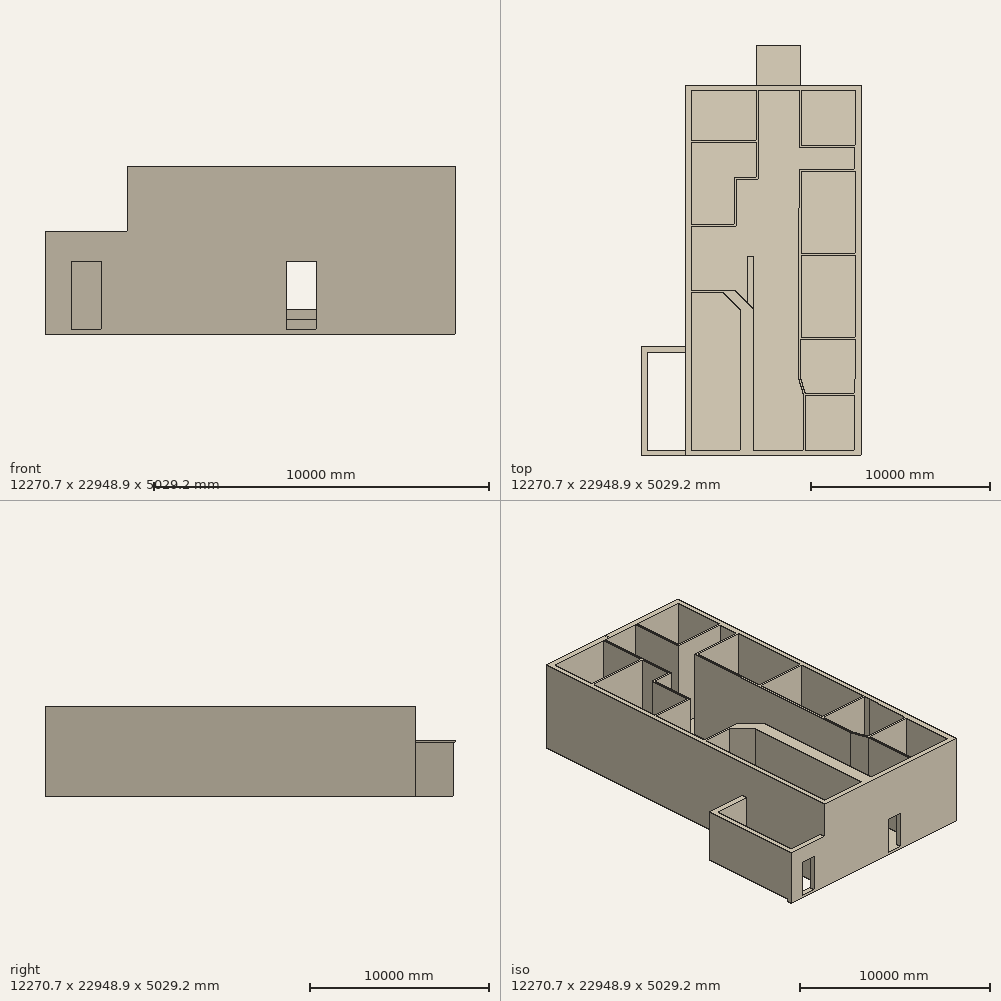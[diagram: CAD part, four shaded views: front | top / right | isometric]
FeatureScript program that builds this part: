
annotation { "Feature Type Name" : "Feature", "Feature Type Description" : "" }
export const myFeature = defineFeature(function(context is Context, id is Id, definition is map)
    precondition{}
    {
        {
            var Q0;
            Q0=qCreatedBy(makeId("Top.planeOp"),FACE);
            var sketch = newSketch(context, id + "F0", { "sketchPlane" : qUnion([Q0])});
            skLineSegment(sketch, "E0.left", {"start": v(4876.8, -10061.6) * mm, "end": v(4876.8, -6899.3) * mm});
            skLineSegment(sketch, "E0.right", {"start": v(2019.3, -10073.92) * mm, "end": v(2019.3, -7013.6) * mm});
            skLineSegment(sketch, "E1.left", {"start": v(4876.8, -6899.3) * mm, "end": v(4930.14, -4203.7) * mm});
            skLineSegment(sketch, "E2.top", {"start": v(4930.14, 835) * mm, "end": v(1882.14, 835) * mm});
            skLineSegment(sketch, "E2.left", {"start": v(4930.14, -4203.7) * mm, "end": v(4930.14, -3851.3) * mm});
            skLineSegment(sketch, "E3.bottom", {"start": v(1882.14, 835) * mm, "end": v(4930.14, 835) * mm});
            skLineSegment(sketch, "E4.bottom", {"start": v(-4267.2, -10061.6) * mm, "end": v(-1524, -10061.6) * mm});
            skLineSegment(sketch, "E4.left", {"start": v(-4267.2, -10061.6) * mm, "end": v(-4267.2, -1222.4) * mm});
            skLineSegment(sketch, "E5", {"start": v(-4267.2, -1222.4) * mm, "end": v(-2489.53, -1222.4) * mm});
            skLineSegment(sketch, "E6.top", {"start": v(-609.6, 5216.5) * mm, "end": v(-1828.8, 5216.5) * mm});
            skLineSegment(sketch, "E6.right", {"start": v(-1828.8, 2574.9) * mm, "end": v(-1828.8, 5216.5) * mm});
            skLineSegment(sketch, "E7", {"start": v(-4267.2, 2574.9) * mm, "end": v(-1828.8, 2574.9) * mm});
            skLineSegment(sketch, "E8", {"start": v(2133.6, -10061.6) * mm, "end": v(2133.6, -7013.6) * mm});
            skLineSegment(sketch, "E9", {"start": v(2133.6, -7013.6) * mm, "end": v(4876.8, -7013.6) * mm});
            skLineSegment(sketch, "E10", {"start": v(2104.72, -6899.3) * mm, "end": v(4876.8, -6899.3) * mm});
            skLineSegment(sketch, "E11", {"start": v(2133.6, -10061.6) * mm, "end": v(4876.8, -10061.6) * mm});
            skLineSegment(sketch, "E12", {"start": v(1882.14, 949.3) * mm, "end": v(1882.14, 5521.3) * mm});
            skLineSegment(sketch, "E13.0", {"start": v(4930.14, -3737) * mm, "end": v(1882.14, -3737) * mm});
            skLineSegment(sketch, "E14.0", {"start": v(4930.14, -3851.3) * mm, "end": v(1840.7, -3851.3) * mm});
            skLineSegment(sketch, "E15", {"start": v(1840.7, -3851.3) * mm, "end": v(1831.42, -5974.23) * mm});
            skLineSegment(sketch, "E16", {"start": v(1882.14, -3737) * mm, "end": v(1882.14, 835) * mm});
            skLineSegment(sketch, "E17.1", {"start": v(-495.3, 5102.2) * mm, "end": v(-1714.5, 5102.2) * mm});
            skLineSegment(sketch, "E18.1", {"start": v(-4267.2, 2460.6) * mm, "end": v(-1714.5, 2460.6) * mm});
            skLineSegment(sketch, "E19", {"start": v(-1714.5, 5102.2) * mm, "end": v(-1714.5, 2460.6) * mm});
            skLineSegment(sketch, "E20", {"start": v(-4267.2, 2460.6) * mm, "end": v(-4267.2, -1108.1) * mm});
            skLineSegment(sketch, "E21", {"start": v(-4267.2, 7146.9) * mm, "end": v(-4267.2, 2574.9) * mm});
            skLineSegment(sketch, "E22", {"start": v(-609.6, 5216.5) * mm, "end": v(-609.6, 7146.9) * mm});
            skLineSegment(sketch, "E23", {"start": v(-4267.2, 7146.9) * mm, "end": v(-609.6, 7146.9) * mm});
            skLineSegment(sketch, "E24", {"start": v(-495.3, 5102.2) * mm, "end": v(-495.3, 10042.5) * mm});
            skLineSegment(sketch, "E25", {"start": v(5234.94, -10366.4) * mm, "end": v(-4581.85, -10366.4) * mm});
            skLineSegment(sketch, "E26", {"start": v(1882.14, 949.3) * mm, "end": v(4930.14, 949.3) * mm});
            skLineSegment(sketch, "E27", {"start": v(4930.14, 949.3) * mm, "end": v(4930.14, 5521.3) * mm});
            skLineSegment(sketch, "E28", {"start": v(4930.14, 5521.3) * mm, "end": v(1882.14, 5521.3) * mm});
            skLineSegment(sketch, "E29.0", {"start": v(-4267.2, 7261.2) * mm, "end": v(-609.6, 7261.2) * mm});
            skLineSegment(sketch, "E30", {"start": v(-609.6, 7261.2) * mm, "end": v(-609.6, 10042.5) * mm});
            skLineSegment(sketch, "E31", {"start": v(-4267.2, 7261.2) * mm, "end": v(-4267.2, 10042.5) * mm});
            skLineSegment(sketch, "E32", {"start": v(-4267.2, 10042.5) * mm, "end": v(-609.6, 10042.5) * mm});
            skLineSegment(sketch, "E33", {"start": v(5234.94, -10366.4) * mm, "end": v(5234.94, 10347.3) * mm});
            skLineSegment(sketch, "E34", {"start": v(1767.84, 5635.6) * mm, "end": v(4876.8, 5635.6) * mm});
            skLineSegment(sketch, "E35", {"start": v(4876.8, 5635.6) * mm, "end": v(4876.8, 6880.2) * mm});
            skLineSegment(sketch, "E36", {"start": v(4876.8, 6880.2) * mm, "end": v(1767.84, 6880.2) * mm});
            skLineSegment(sketch, "E37", {"start": v(4930.14, 6994.5) * mm, "end": v(4930.14, 10042.5) * mm});
            skLineSegment(sketch, "E38", {"start": v(4930.14, 6994.5) * mm, "end": v(1882.14, 6994.5) * mm});
            skLineSegment(sketch, "E39", {"start": v(1882.14, 6994.5) * mm, "end": v(1882.14, 10042.5) * mm});
            skLineSegment(sketch, "E40", {"start": v(4930.14, 10042.5) * mm, "end": v(1882.14, 10042.5) * mm});
            skLineSegment(sketch, "E41", {"start": v(1767.84, 6880.2) * mm, "end": v(1767.84, 10042.5) * mm});
            skLineSegment(sketch, "E42", {"start": v(1767.84, 10347.3) * mm, "end": v(5234.94, 10347.3) * mm});
            skLineSegment(sketch, "E43.0", {"start": v(-4572, -10061.6) * mm, "end": v(-4572, -4575.2) * mm});
            skLineSegment(sketch, "E44", {"start": v(-4581.85, -10366.4) * mm, "end": v(-7035.8, -10366.4) * mm});
            skLineSegment(sketch, "E45", {"start": v(-4572, -4575.2) * mm, "end": v(-6731, -4575.2) * mm});
            skLineSegment(sketch, "E46", {"start": v(-6731, -4575.2) * mm, "end": v(-6731, -10061.6) * mm});
            skLineSegment(sketch, "E47.0", {"start": v(-7035.8, -4270.4) * mm, "end": v(-7035.8, -10366.4) * mm});
            skLineSegment(sketch, "E47.1", {"start": v(-4572, -4270.4) * mm, "end": v(-7035.8, -4270.4) * mm});
            skLineSegment(sketch, "E48", {"start": v(-4572, -10061.6) * mm, "end": v(-6731, -10061.6) * mm});
            skLineSegment(sketch, "E49.trimOffspring", {"start": v(4930.14, -3737) * mm, "end": v(4930.14, 835) * mm});
            skLineSegment(sketch, "E50", {"start": v(1717.04, -5990.52) * mm, "end": v(1767.84, 5635.6) * mm});
            skLineSegment(sketch, "E51", {"start": v(-4572, -4270.4) * mm, "end": v(-4572, 10347.3) * mm});
            skLineSegment(sketch, "E52", {"start": v(-4572, 10347.3) * mm, "end": v(-495.3, 10347.3) * mm});
            skLineSegment(sketch, "E53", {"start": v(-800.1, -10061.6) * mm, "end": v(2019.3, -10073.92) * mm});
            skLineSegment(sketch, "E54", {"start": v(-495.3, 10347.3) * mm, "end": v(-495.3, 12480.9) * mm});
            skLineSegment(sketch, "E55", {"start": v(-495.3, 12480.9) * mm, "end": v(1767.84, 12480.9) * mm});
            skLineSegment(sketch, "E56", {"start": v(1767.84, 12480.9) * mm, "end": v(1767.84, 10347.3) * mm});
            skLineSegment(sketch, "E57.0", {"start": v(1463.04, 12176.1) * mm, "end": v(1463.04, 10347.3) * mm});
            skLineSegment(sketch, "E57.1", {"start": v(-190.5, 12176.1) * mm, "end": v(1463.04, 12176.1) * mm});
            skLineSegment(sketch, "E57.2", {"start": v(-190.5, 10347.3) * mm, "end": v(-190.5, 12176.1) * mm});
            skLineSegment(sketch, "E58", {"start": v(-495.3, 10042.5) * mm, "end": v(-190.5, 10042.5) * mm});
            skLineSegment(sketch, "E59", {"start": v(-190.5, 10042.5) * mm, "end": v(-190.5, 10347.3) * mm});
            skLineSegment(sketch, "E60", {"start": v(1882.14, 10042.5) * mm, "end": v(1463.04, 10042.5) * mm});
            skLineSegment(sketch, "E61", {"start": v(1463.04, 10042.5) * mm, "end": v(1463.04, 10347.3) * mm});
            skLineSegment(sketch, "E62", {"start": v(2019.3, -7013.6) * mm, "end": v(1717.04, -5990.52) * mm});
            skLineSegment(sketch, "E63.0", {"start": v(2104.72, -6899.3) * mm, "end": v(1831.42, -5974.23) * mm});
            skLineSegment(sketch, "E64", {"start": v(1717.04, -5990.52) * mm, "end": v(1868.17, -6502.06) * mm});
            skLineSegment(sketch, "E65", {"start": v(-2489.53, -1222.4) * mm, "end": v(-1524, -2187.93) * mm});
            skLineSegment(sketch, "E66.1", {"start": v(-1832.58, -1108.1) * mm, "end": v(-800.1, -2140.58) * mm});
            skLineSegment(sketch, "E67", {"start": v(-800.1, -10061.6) * mm, "end": v(-800.1, -2140.58) * mm});
            skLineSegment(sketch, "E68", {"start": v(-1524, -10061.6) * mm, "end": v(-1524, -2187.93) * mm});
            skLineSegment(sketch, "E69", {"start": v(-4267.2, -1108.1) * mm, "end": v(-1832.58, -1108.1) * mm});
            skSolve(sketch);
        }
        {
            var Q0;
            {var subQ3=sQuery(id+"F0.wireOp",EDGE,"E0.right");Q0=makeQuery(id+"F0.imprint","IMPRINT",FACE,{"disambiguationData":[TD([[makeQuery(id+"F0.imprint","IMPRINT",EDGE,{"derivedFrom":subQ3}),-1.0]])]});}
            extrude(context, id + "F1", {"entities" : qUnion([Q0]), "depth" : 4876.8 * mm, "offsetDistance" : 25.4 * mm});
        }
        {
            var Q0;
            Q0=makeQuery(id+"F1.opExtrude","CAP_FACE",FACE,{"disambiguationData":[OSD([sQuery(id+"F0.wireOp",EDGE,"E0.left"),sQuery(id+"F0.wireOp",EDGE,"E0.right"),sQuery(id+"F0.wireOp",EDGE,"E1.left"),sQuery(id+"F0.wireOp",EDGE,"E2.left"),sQuery(id+"F0.wireOp",EDGE,"E3.bottom"),sQuery(id+"F0.wireOp",EDGE,"E4.bottom"),sQuery(id+"F0.wireOp",EDGE,"E4.left"),sQuery(id+"F0.wireOp",EDGE,"lTb8aQtv-XThL-iinc-JPeR-yFG4zokSqyV0"),sQuery(id+"F0.wireOp",EDGE,"okg78HFr-gpBt-xwTH-bfG1-MK0WquynLWe5"),sQuery(id+"F0.wireOp",EDGE,"E5"),sQuery(id+"F0.wireOp",EDGE,"E6.top"),sQuery(id+"F0.wireOp",EDGE,"E6.right"),sQuery(id+"F0.wireOp",EDGE,"E7"),sQuery(id+"F0.wireOp",EDGE,"E8"),sQuery(id+"F0.wireOp",EDGE,"E9"),sQuery(id+"F0.wireOp",EDGE,"E10"),sQuery(id+"F0.wireOp",EDGE,"E11"),sQuery(id+"F0.wireOp",EDGE,"627e6cba-16d0-459f-a526-ef50462c6f62.0"),sQuery(id+"F0.wireOp",EDGE,"627e6cba-16d0-459f-a526-ef50462c6f62.1"),sQuery(id+"F0.wireOp",EDGE,"627e6cba-16d0-459f-a526-ef50462c6f62.2"),sQuery(id+"F0.wireOp",EDGE,"E12"),sQuery(id+"F0.wireOp",EDGE,"E13.0"),sQuery(id+"F0.wireOp",EDGE,"E14.0"),sQuery(id+"F0.wireOp",EDGE,"E15"),sQuery(id+"F0.wireOp",EDGE,"E16"),sQuery(id+"F0.wireOp",EDGE,"E17.1"),sQuery(id+"F0.wireOp",EDGE,"E18.1"),sQuery(id+"F0.wireOp",EDGE,"E19"),sQuery(id+"F0.wireOp",EDGE,"E20"),sQuery(id+"F0.wireOp",EDGE,"E21"),sQuery(id+"F0.wireOp",EDGE,"E22"),sQuery(id+"F0.wireOp",EDGE,"E23"),sQuery(id+"F0.wireOp",EDGE,"E24"),sQuery(id+"F0.wireOp",EDGE,"E25"),sQuery(id+"F0.wireOp",EDGE,"E26"),sQuery(id+"F0.wireOp",EDGE,"E27"),sQuery(id+"F0.wireOp",EDGE,"E28"),sQuery(id+"F0.wireOp",EDGE,"E29.0"),sQuery(id+"F0.wireOp",EDGE,"E30"),sQuery(id+"F0.wireOp",EDGE,"E31"),sQuery(id+"F0.wireOp",EDGE,"E32"),sQuery(id+"F0.wireOp",EDGE,"E33"),sQuery(id+"F0.wireOp",EDGE,"E34"),sQuery(id+"F0.wireOp",EDGE,"E35"),sQuery(id+"F0.wireOp",EDGE,"E36"),sQuery(id+"F0.wireOp",EDGE,"E37"),sQuery(id+"F0.wireOp",EDGE,"E38"),sQuery(id+"F0.wireOp",EDGE,"E39"),sQuery(id+"F0.wireOp",EDGE,"E40"),sQuery(id+"F0.wireOp",EDGE,"E41"),sQuery(id+"F0.wireOp",EDGE,"E42"),sQuery(id+"F0.wireOp",EDGE,"E43.0"),sQuery(id+"F0.wireOp",EDGE,"E44"),sQuery(id+"F0.wireOp",EDGE,"E45"),sQuery(id+"F0.wireOp",EDGE,"E46"),sQuery(id+"F0.wireOp",EDGE,"E47.0"),sQuery(id+"F0.wireOp",EDGE,"E47.1"),sQuery(id+"F0.wireOp",EDGE,"E48"),sQuery(id+"F0.wireOp",EDGE,"E49.trimOffspring"),sQuery(id+"F0.wireOp",EDGE,"E50"),sQuery(id+"F0.wireOp",EDGE,"E51"),sQuery(id+"F0.wireOp",EDGE,"E52"),sQuery(id+"F0.wireOp",EDGE,"E53"),sQuery(id+"F0.wireOp",EDGE,"q5LcNnRt-usUO-qFZe-bVMC-yrK6j8Ch3Ls0"),sQuery(id+"F0.wireOp",EDGE,"5e3MKgz6-kyOg-u4VT-bwkN-dNsQbsID09DU"),sQuery(id+"F0.wireOp",EDGE,"E54"),sQuery(id+"F0.wireOp",EDGE,"E55"),sQuery(id+"F0.wireOp",EDGE,"E56"),sQuery(id+"F0.wireOp",EDGE,"E57.0"),sQuery(id+"F0.wireOp",EDGE,"E57.1"),sQuery(id+"F0.wireOp",EDGE,"E57.2"),sQuery(id+"F0.wireOp",EDGE,"JoGApFtb-8rWJ-i2tt-OxZK-aDool6YSFolw"),sQuery(id+"F0.wireOp",EDGE,"hMZSVZbt-OIxk-Dhpj-C3v7-He4Mro5a6Fzq")])],"isStart":true});
            var sketch = newSketch(context, id + "F2", { "sketchPlane" : qUnion([Q0])});
            skLineSegment(sketch, "E70.right", {"start": v(-4572, 10366.4) * mm, "end": v(-4572, 4270.4) * mm});
            skLineSegment(sketch, "E71.bottom", {"start": v(5234.94, 10366.4) * mm, "end": v(-4572, 10366.4) * mm});
            skLineSegment(sketch, "E71.top", {"start": v(5234.94, -10347.3) * mm, "end": v(1767.84, -10347.3) * mm});
            skLineSegment(sketch, "E71.left", {"start": v(5234.94, 10366.4) * mm, "end": v(5234.94, -10347.3) * mm});
            skLineSegment(sketch, "E71.right", {"start": v(-4572, 4270.4) * mm, "end": v(-4572, -10347.3) * mm});
            skLineSegment(sketch, "E72.bottom", {"start": v(1767.84, -12480.9) * mm, "end": v(-495.3, -12480.9) * mm});
            skLineSegment(sketch, "E72.left", {"start": v(1767.84, -12480.9) * mm, "end": v(1767.84, -10347.3) * mm});
            skLineSegment(sketch, "E72.right", {"start": v(-495.3, -12480.9) * mm, "end": v(-495.3, -10347.3) * mm});
            skLineSegment(sketch, "E73.trimOffspring", {"start": v(-495.3, -10347.3) * mm, "end": v(-4572, -10347.3) * mm});
            skSolve(sketch);
        }
        {
            var Q0;
            Q0 = qSketchRegion(id + "F2", true);
            extrude(context, id + "F3", {"entities" : qUnion([Q0]), "operationType" : NewBodyOperationType.ADD, "depth" : 152.4 * mm, "offsetDistance" : 25.4 * mm});
        }
        {
            var Q0;
            Q0=makeQuery(id+"F3.boolean.opBoolean","SPLIT",FACE,{"disambiguationData":[TD([makeQuery(id+"F1.opExtrude","SWEPT_FACE",FACE,{"disambiguationData":[OSD([sQuery(id+"F0.wireOp",EDGE,"E0.right")])]})])],"derivedFrom":makeQuery(id+"F3.opExtrude","CAP_FACE",FACE,{"disambiguationData":[OSD([sQuery(id+"F2.wireOp",EDGE,"E70.right"),sQuery(id+"F2.wireOp",EDGE,"E71.bottom"),sQuery(id+"F2.wireOp",EDGE,"E71.top"),sQuery(id+"F2.wireOp",EDGE,"E71.left"),sQuery(id+"F2.wireOp",EDGE,"E71.right"),sQuery(id+"F2.wireOp",EDGE,"E72.bottom"),sQuery(id+"F2.wireOp",EDGE,"E72.left"),sQuery(id+"F2.wireOp",EDGE,"E72.right"),sQuery(id+"F2.wireOp",EDGE,"E73.trimOffspring")])],"isStart":true})});
            var sketch = newSketch(context, id + "F4", { "sketchPlane" : qUnion([Q0])});
            skLineSegment(sketch, "E74.bottom", {"start": v(-190.5, 12176.1) * mm, "end": v(1463.04, 12176.1) * mm});
            skLineSegment(sketch, "E74.top", {"start": v(-190.5, 10042.5) * mm, "end": v(1463.04, 10042.5) * mm});
            skLineSegment(sketch, "E74.left", {"start": v(-190.5, 12176.1) * mm, "end": v(-190.5, 10042.5) * mm});
            skLineSegment(sketch, "E74.right", {"start": v(1463.04, 12176.1) * mm, "end": v(1463.04, 10042.5) * mm});
            skSolve(sketch);
        }
        {
            var Q0;
            Q0=makeQuery(id+"F4.imprint","IMPRINT",FACE,{"disambiguationData":[TD([[makeQuery(id+"F4.imprint","IMPRINT",EDGE,{"derivedFrom":sQuery(id+"F4.wireOp",EDGE,"E74.bottom")}),-1.0]])]});
            extrude(context, id + "F5", {"entities" : qUnion([Q0]), "operationType" : NewBodyOperationType.ADD, "depth" : 304.8 * mm, "offsetDistance" : 25.4 * mm});
        }
        {
            var Q0;
            Q0=makeQuery(id+"F5.opExtrude","CAP_FACE",FACE,{"disambiguationData":[OSD([sQuery(id+"F4.wireOp",EDGE,"E74.bottom"),sQuery(id+"F4.wireOp",EDGE,"E74.top"),sQuery(id+"F4.wireOp",EDGE,"E74.left"),sQuery(id+"F4.wireOp",EDGE,"E74.right")])],"isStart":false});
            var sketch = newSketch(context, id + "F6", { "sketchPlane" : qUnion([Q0])});
            skLineSegment(sketch, "E75.bottom", {"start": v(-190.5, 12176.1) * mm, "end": v(1463.04, 12176.1) * mm});
            skLineSegment(sketch, "E75.top", {"start": v(-190.5, 10804.5) * mm, "end": v(1463.04, 10804.5) * mm});
            skLineSegment(sketch, "E75.left", {"start": v(-190.5, 12176.1) * mm, "end": v(-190.5, 10804.5) * mm});
            skLineSegment(sketch, "E75.right", {"start": v(1463.04, 12176.1) * mm, "end": v(1463.04, 10804.5) * mm});
            skSolve(sketch);
        }
        {
            var Q0;
            Q0=makeQuery(id+"F6.imprint","IMPRINT",FACE,{"disambiguationData":[TD([[makeQuery(id+"F6.imprint","IMPRINT",EDGE,{"derivedFrom":sQuery(id+"F6.wireOp",EDGE,"E75.bottom")}),-1.0]])]});
            extrude(context, id + "F7", {"entities" : qUnion([Q0]), "operationType" : NewBodyOperationType.ADD, "depth" : 304.8 * mm, "offsetDistance" : 25.4 * mm});
        }
        {
            var Q0;
            Q0=makeQuery(id+"F1.opExtrude","SWEPT_FACE",FACE,{"disambiguationData":[OSD([sQuery(id+"F0.wireOp",EDGE,"E57.1")])]});
            var sketch = newSketch(context, id + "F8", { "sketchPlane" : qUnion([Q0])});
            skLineSegment(sketch, "E76.top", {"start": v(165.1, 609.6) * mm, "end": v(1107.44, 609.6) * mm});
            skLineSegment(sketch, "E76.left", {"start": v(165.1, 2641.6) * mm, "end": v(165.1, 609.6) * mm});
            skLineSegment(sketch, "E76.right", {"start": v(1107.44, 2641.6) * mm, "end": v(1107.44, 609.6) * mm});
            skLineSegment(sketch, "E77", {"start": v(165.1, 2641.6) * mm, "end": v(1107.44, 2641.6) * mm});
            skSolve(sketch);
        }
        {
            var Q0;
            Q0=makeQuery(id+"F8.imprint","IMPRINT",FACE,{"disambiguationData":[TD([[makeQuery(id+"F8.imprint","IMPRINT",EDGE,{"derivedFrom":sQuery(id+"F8.wireOp",EDGE,"E76.left")}),1.0]])]});
            extrude(context, id + "F9", {"entities" : qUnion([Q0]), "operationType" : NewBodyOperationType.REMOVE, "oppositeDirection" : true, "depth" : 304.8 * mm, "offsetDistance" : 25.4 * mm});
        }
        {
            var Q0;
            Q0=makeQuery(id+"F1.opExtrude","CAP_FACE",FACE,{"disambiguationData":[OSD([sQuery(id+"F0.wireOp",EDGE,"E0.left"),sQuery(id+"F0.wireOp",EDGE,"E0.right"),sQuery(id+"F0.wireOp",EDGE,"E1.left"),sQuery(id+"F0.wireOp",EDGE,"E2.left"),sQuery(id+"F0.wireOp",EDGE,"E3.bottom"),sQuery(id+"F0.wireOp",EDGE,"E4.bottom"),sQuery(id+"F0.wireOp",EDGE,"E4.left"),sQuery(id+"F0.wireOp",EDGE,"lTb8aQtv-XThL-iinc-JPeR-yFG4zokSqyV0"),sQuery(id+"F0.wireOp",EDGE,"okg78HFr-gpBt-xwTH-bfG1-MK0WquynLWe5"),sQuery(id+"F0.wireOp",EDGE,"E5"),sQuery(id+"F0.wireOp",EDGE,"E6.top"),sQuery(id+"F0.wireOp",EDGE,"E6.right"),sQuery(id+"F0.wireOp",EDGE,"E7"),sQuery(id+"F0.wireOp",EDGE,"E8"),sQuery(id+"F0.wireOp",EDGE,"E9"),sQuery(id+"F0.wireOp",EDGE,"E10"),sQuery(id+"F0.wireOp",EDGE,"E11"),sQuery(id+"F0.wireOp",EDGE,"627e6cba-16d0-459f-a526-ef50462c6f62.0"),sQuery(id+"F0.wireOp",EDGE,"627e6cba-16d0-459f-a526-ef50462c6f62.1"),sQuery(id+"F0.wireOp",EDGE,"627e6cba-16d0-459f-a526-ef50462c6f62.2"),sQuery(id+"F0.wireOp",EDGE,"E12"),sQuery(id+"F0.wireOp",EDGE,"E13.0"),sQuery(id+"F0.wireOp",EDGE,"E14.0"),sQuery(id+"F0.wireOp",EDGE,"E15"),sQuery(id+"F0.wireOp",EDGE,"E16"),sQuery(id+"F0.wireOp",EDGE,"E17.1"),sQuery(id+"F0.wireOp",EDGE,"E18.1"),sQuery(id+"F0.wireOp",EDGE,"E19"),sQuery(id+"F0.wireOp",EDGE,"E20"),sQuery(id+"F0.wireOp",EDGE,"E21"),sQuery(id+"F0.wireOp",EDGE,"E22"),sQuery(id+"F0.wireOp",EDGE,"E23"),sQuery(id+"F0.wireOp",EDGE,"E24"),sQuery(id+"F0.wireOp",EDGE,"E25"),sQuery(id+"F0.wireOp",EDGE,"E26"),sQuery(id+"F0.wireOp",EDGE,"E27"),sQuery(id+"F0.wireOp",EDGE,"E28"),sQuery(id+"F0.wireOp",EDGE,"E29.0"),sQuery(id+"F0.wireOp",EDGE,"E30"),sQuery(id+"F0.wireOp",EDGE,"E31"),sQuery(id+"F0.wireOp",EDGE,"E32"),sQuery(id+"F0.wireOp",EDGE,"E33"),sQuery(id+"F0.wireOp",EDGE,"E34"),sQuery(id+"F0.wireOp",EDGE,"E35"),sQuery(id+"F0.wireOp",EDGE,"E36"),sQuery(id+"F0.wireOp",EDGE,"E37"),sQuery(id+"F0.wireOp",EDGE,"E38"),sQuery(id+"F0.wireOp",EDGE,"E39"),sQuery(id+"F0.wireOp",EDGE,"E40"),sQuery(id+"F0.wireOp",EDGE,"E41"),sQuery(id+"F0.wireOp",EDGE,"E42"),sQuery(id+"F0.wireOp",EDGE,"E43.0"),sQuery(id+"F0.wireOp",EDGE,"E44"),sQuery(id+"F0.wireOp",EDGE,"E45"),sQuery(id+"F0.wireOp",EDGE,"E46"),sQuery(id+"F0.wireOp",EDGE,"E47.0"),sQuery(id+"F0.wireOp",EDGE,"E47.1"),sQuery(id+"F0.wireOp",EDGE,"E48"),sQuery(id+"F0.wireOp",EDGE,"E49.trimOffspring"),sQuery(id+"F0.wireOp",EDGE,"E50"),sQuery(id+"F0.wireOp",EDGE,"E51"),sQuery(id+"F0.wireOp",EDGE,"E52"),sQuery(id+"F0.wireOp",EDGE,"E53"),sQuery(id+"F0.wireOp",EDGE,"q5LcNnRt-usUO-qFZe-bVMC-yrK6j8Ch3Ls0"),sQuery(id+"F0.wireOp",EDGE,"5e3MKgz6-kyOg-u4VT-bwkN-dNsQbsID09DU"),sQuery(id+"F0.wireOp",EDGE,"E54"),sQuery(id+"F0.wireOp",EDGE,"E55"),sQuery(id+"F0.wireOp",EDGE,"E56"),sQuery(id+"F0.wireOp",EDGE,"E57.0"),sQuery(id+"F0.wireOp",EDGE,"E57.1"),sQuery(id+"F0.wireOp",EDGE,"E57.2"),sQuery(id+"F0.wireOp",EDGE,"E58"),sQuery(id+"F0.wireOp",EDGE,"E59"),sQuery(id+"F0.wireOp",EDGE,"E60"),sQuery(id+"F0.wireOp",EDGE,"E61")])],"isStart":false});
            var sketch = newSketch(context, id + "F10", { "sketchPlane" : qUnion([Q0])});
            skLineSegment(sketch, "E78.bottom", {"start": v(1767.84, 10347.3) * mm, "end": v(-495.3, 10347.3) * mm});
            skLineSegment(sketch, "E78.top", {"start": v(1767.84, 12480.9) * mm, "end": v(-495.3, 12480.9) * mm});
            skLineSegment(sketch, "E78.left", {"start": v(1767.84, 10347.3) * mm, "end": v(1767.84, 12480.9) * mm});
            skLineSegment(sketch, "E78.right", {"start": v(-495.3, 10347.3) * mm, "end": v(-495.3, 12480.9) * mm});
            skSolve(sketch);
        }
        {
            var Q0;
            Q0=makeQuery(id+"F10.imprint","IMPRINT",FACE,{"disambiguationData":[TD([[makeQuery(id+"F10.imprint","IMPRINT",EDGE,{"derivedFrom":sQuery(id+"F10.wireOp",EDGE,"E78.top")}),-1.0]])]});
            extrude(context, id + "F11", {"entities" : qUnion([Q0]), "operationType" : NewBodyOperationType.REMOVE, "oppositeDirection" : true, "depth" : 2032 * mm, "offsetDistance" : 25.4 * mm});
        }
        {
            var Q0;
            Q0=makeQuery(id+"F11.boolean.opBoolean","COPY",FACE,{"derivedFrom":makeQuery(id+"F11.opExtrude","CAP_FACE",FACE,{"disambiguationData":[OSD([sQuery(id+"F0.wireOp",EDGE,"E57.0"),sQuery(id+"F0.wireOp",EDGE,"E57.1"),sQuery(id+"F0.wireOp",EDGE,"E57.2"),sQuery(id+"F0.wireOp",EDGE,"E59"),sQuery(id+"F0.wireOp",EDGE,"E61"),sQuery(id+"F10.wireOp",EDGE,"E78.bottom"),sQuery(id+"F10.wireOp",EDGE,"E78.top"),sQuery(id+"F10.wireOp",EDGE,"E78.left"),sQuery(id+"F10.wireOp",EDGE,"E78.right")])],"isStart":false})});
            var sketch = newSketch(context, id + "F12", { "sketchPlane" : qUnion([Q0])});
            skLineSegment(sketch, "E79.4", {"start": v(1817.65, 10347.3) * mm, "end": v(1817.65, 12582.5) * mm});
            skLineSegment(sketch, "E79.5", {"start": v(1817.65, 12582.5) * mm, "end": v(-596.9, 12582.5) * mm});
            skLineSegment(sketch, "E79.6", {"start": v(-596.9, 12582.5) * mm, "end": v(-596.9, 10347.3) * mm});
            skLineSegment(sketch, "E80", {"start": v(1309.65, 10347.3) * mm, "end": v(1817.65, 10347.3) * mm});
            skLineSegment(sketch, "E81", {"start": v(-88.9, 10347.3) * mm, "end": v(-596.9, 10347.3) * mm});
            skLineSegment(sketch, "E82", {"start": v(1817.65, 10347.3) * mm, "end": v(-596.9, 10347.3) * mm});
            skSolve(sketch);
        }
        {
            var Q0;
            Q0 = qSketchRegion(id + "F12", true);
            extrude(context, id + "F13", {"entities" : qUnion([Q0]), "operationType" : NewBodyOperationType.ADD, "depth" : 152.4 * mm, "offsetDistance" : 25.4 * mm});
        }
        {
            var Q0;
            Q0=makeQuery(id+"F1.opExtrude","SWEPT_FACE",FACE,{"disambiguationData":[OSD([sQuery(id+"F0.wireOp",EDGE,"E57.0"),sQuery(id+"F0.wireOp",EDGE,"E61")])]});
            var sketch = newSketch(context, id + "F14", { "sketchPlane" : qUnion([Q0])});
            skLineSegment(sketch, "E83.bottom", {"start": v(-10042.5, 4876.8) * mm, "end": v(-10347.3, 4876.8) * mm});
            skLineSegment(sketch, "E83.left", {"start": v(-10042.5, 4876.8) * mm, "end": v(-10042.5, 4165.6) * mm});
            skLineSegment(sketch, "E83.right", {"start": v(-10347.3, 4876.8) * mm, "end": v(-10347.3, 2997.2) * mm});
            skLineSegment(sketch, "E84.bottom", {"start": v(-10347.3, 2844.8) * mm, "end": v(-10042.5, 2844.8) * mm});
            skLineSegment(sketch, "E84.left", {"start": v(-10347.3, 2844.8) * mm, "end": v(-10347.3, 2997.2) * mm});
            skLineSegment(sketch, "E84.right", {"start": v(-10042.5, 2844.8) * mm, "end": v(-10042.5, 4165.6) * mm});
            skSolve(sketch);
        }
        {
            var Q0;
            Q0=makeQuery(id+"F14.imprint","IMPRINT",FACE,{"disambiguationData":[TD([[makeQuery(id+"F14.imprint","IMPRINT",EDGE,{"derivedFrom":sQuery(id+"F14.wireOp",EDGE,"E83.bottom")}),-1.0]])]});
            extrude(context, id + "F15", {"entities" : qUnion([Q0]), "operationType" : NewBodyOperationType.ADD, "depth" : 1625.6 * mm, "offsetDistance" : 25.4 * mm});
        }
        {
            var Q0;
            Q0=makeQuery(id+"F15.boolean.opBoolean","MERGE",FACE,{"derivedFrom":[makeQuery(id+"F1.opExtrude","CAP_FACE",FACE,{"disambiguationData":[OSD([sQuery(id+"F0.wireOp",EDGE,"E0.left"),sQuery(id+"F0.wireOp",EDGE,"E0.right"),sQuery(id+"F0.wireOp",EDGE,"E1.left"),sQuery(id+"F0.wireOp",EDGE,"E2.left"),sQuery(id+"F0.wireOp",EDGE,"E3.bottom"),sQuery(id+"F0.wireOp",EDGE,"E4.bottom"),sQuery(id+"F0.wireOp",EDGE,"E4.left"),sQuery(id+"F0.wireOp",EDGE,"lTb8aQtv-XThL-iinc-JPeR-yFG4zokSqyV0"),sQuery(id+"F0.wireOp",EDGE,"okg78HFr-gpBt-xwTH-bfG1-MK0WquynLWe5"),sQuery(id+"F0.wireOp",EDGE,"E5"),sQuery(id+"F0.wireOp",EDGE,"E6.top"),sQuery(id+"F0.wireOp",EDGE,"E6.right"),sQuery(id+"F0.wireOp",EDGE,"E7"),sQuery(id+"F0.wireOp",EDGE,"E8"),sQuery(id+"F0.wireOp",EDGE,"E9"),sQuery(id+"F0.wireOp",EDGE,"E10"),sQuery(id+"F0.wireOp",EDGE,"E11"),sQuery(id+"F0.wireOp",EDGE,"627e6cba-16d0-459f-a526-ef50462c6f62.0"),sQuery(id+"F0.wireOp",EDGE,"627e6cba-16d0-459f-a526-ef50462c6f62.1"),sQuery(id+"F0.wireOp",EDGE,"627e6cba-16d0-459f-a526-ef50462c6f62.2"),sQuery(id+"F0.wireOp",EDGE,"E12"),sQuery(id+"F0.wireOp",EDGE,"E13.0"),sQuery(id+"F0.wireOp",EDGE,"E14.0"),sQuery(id+"F0.wireOp",EDGE,"E15"),sQuery(id+"F0.wireOp",EDGE,"E16"),sQuery(id+"F0.wireOp",EDGE,"E17.1"),sQuery(id+"F0.wireOp",EDGE,"E18.1"),sQuery(id+"F0.wireOp",EDGE,"E19"),sQuery(id+"F0.wireOp",EDGE,"E20"),sQuery(id+"F0.wireOp",EDGE,"E21"),sQuery(id+"F0.wireOp",EDGE,"E22"),sQuery(id+"F0.wireOp",EDGE,"E23"),sQuery(id+"F0.wireOp",EDGE,"E24"),sQuery(id+"F0.wireOp",EDGE,"E25"),sQuery(id+"F0.wireOp",EDGE,"E26"),sQuery(id+"F0.wireOp",EDGE,"E27"),sQuery(id+"F0.wireOp",EDGE,"E28"),sQuery(id+"F0.wireOp",EDGE,"E29.0"),sQuery(id+"F0.wireOp",EDGE,"E30"),sQuery(id+"F0.wireOp",EDGE,"E31"),sQuery(id+"F0.wireOp",EDGE,"E32"),sQuery(id+"F0.wireOp",EDGE,"E33"),sQuery(id+"F0.wireOp",EDGE,"E34"),sQuery(id+"F0.wireOp",EDGE,"E35"),sQuery(id+"F0.wireOp",EDGE,"E36"),sQuery(id+"F0.wireOp",EDGE,"E37"),sQuery(id+"F0.wireOp",EDGE,"E38"),sQuery(id+"F0.wireOp",EDGE,"E39"),sQuery(id+"F0.wireOp",EDGE,"E40"),sQuery(id+"F0.wireOp",EDGE,"E41"),sQuery(id+"F0.wireOp",EDGE,"E42"),sQuery(id+"F0.wireOp",EDGE,"E43.0"),sQuery(id+"F0.wireOp",EDGE,"E44"),sQuery(id+"F0.wireOp",EDGE,"E45"),sQuery(id+"F0.wireOp",EDGE,"E46"),sQuery(id+"F0.wireOp",EDGE,"E47.0"),sQuery(id+"F0.wireOp",EDGE,"E47.1"),sQuery(id+"F0.wireOp",EDGE,"E48"),sQuery(id+"F0.wireOp",EDGE,"E49.trimOffspring"),sQuery(id+"F0.wireOp",EDGE,"E50"),sQuery(id+"F0.wireOp",EDGE,"E51"),sQuery(id+"F0.wireOp",EDGE,"E52"),sQuery(id+"F0.wireOp",EDGE,"E53"),sQuery(id+"F0.wireOp",EDGE,"q5LcNnRt-usUO-qFZe-bVMC-yrK6j8Ch3Ls0"),sQuery(id+"F0.wireOp",EDGE,"5e3MKgz6-kyOg-u4VT-bwkN-dNsQbsID09DU"),sQuery(id+"F0.wireOp",EDGE,"E54"),sQuery(id+"F0.wireOp",EDGE,"E55"),sQuery(id+"F0.wireOp",EDGE,"E56"),sQuery(id+"F0.wireOp",EDGE,"E57.0"),sQuery(id+"F0.wireOp",EDGE,"E57.1"),sQuery(id+"F0.wireOp",EDGE,"E57.2"),sQuery(id+"F0.wireOp",EDGE,"E58"),sQuery(id+"F0.wireOp",EDGE,"E59"),sQuery(id+"F0.wireOp",EDGE,"E60"),sQuery(id+"F0.wireOp",EDGE,"E61")])],"isStart":false}),makeQuery(id+"F15.opExtrude","SWEPT_FACE",FACE,{"disambiguationData":[OSD([sQuery(id+"F14.wireOp",EDGE,"E83.bottom")])]})]});
            var sketch = newSketch(context, id + "F16", { "sketchPlane" : qUnion([Q0])});
            skLineSegment(sketch, "E85.bottom", {"start": v(-7035.8, -4270.4) * mm, "end": v(-4572, -4270.4) * mm});
            skLineSegment(sketch, "E85.top", {"start": v(-7035.8, -10366.4) * mm, "end": v(-4572, -10366.4) * mm});
            skLineSegment(sketch, "E85.left", {"start": v(-7035.8, -4270.4) * mm, "end": v(-7035.8, -10366.4) * mm});
            skLineSegment(sketch, "E85.right", {"start": v(-4572, -4270.4) * mm, "end": v(-4572, -10366.4) * mm});
            skSolve(sketch);
        }
        {
            var Q0;
            Q0 = qSketchRegion(id + "F16", true);
            extrude(context, id + "F17", {"entities" : qUnion([Q0]), "operationType" : NewBodyOperationType.REMOVE, "oppositeDirection" : true, "depth" : 1950.72 * mm, "offsetDistance" : 25.4 * mm});
        }
        {
            var Q0;
            Q0=makeQuery(id+"F3.boolean.opBoolean","MERGE",FACE,{"derivedFrom":[makeQuery(id+"F1.opExtrude","SWEPT_FACE",FACE,{"disambiguationData":[OSD([sQuery(id+"F0.wireOp",EDGE,"E25"),sQuery(id+"F0.wireOp",EDGE,"E44")])]}),makeQuery(id+"F3.opExtrude","SWEPT_FACE",FACE,{"disambiguationData":[OSD([sQuery(id+"F2.wireOp",EDGE,"E71.bottom")])]})]});
            var sketch = newSketch(context, id + "F18", { "sketchPlane" : qUnion([Q0])});
            skLineSegment(sketch, "E86.bottom", {"start": v(-7035.8, 2926.08) * mm, "end": v(-4572, 2926.08) * mm});
            skLineSegment(sketch, "E86.top", {"start": v(-7035.8, 0) * mm, "end": v(-4572, 0) * mm});
            skLineSegment(sketch, "E86.left", {"start": v(-7035.8, 2926.08) * mm, "end": v(-7035.8, 0) * mm});
            skLineSegment(sketch, "E86.right", {"start": v(-4572, 2926.08) * mm, "end": v(-4572, 0) * mm});
            skLineSegment(sketch, "E87", {"start": v(-7035.8, 2032) * mm, "end": v(-4572, 2032) * mm});
            skLineSegment(sketch, "E88", {"start": v(-6261.1, 2032) * mm, "end": v(-6261.1, 0) * mm});
            skLineSegment(sketch, "E89", {"start": v(-6261.1, 0) * mm, "end": v(-5346.7, 0) * mm});
            skLineSegment(sketch, "E90", {"start": v(-5346.7, 0) * mm, "end": v(-5346.7, 2032) * mm});
            skLineSegment(sketch, "E91", {"start": v(-5346.7, 2032) * mm, "end": v(-6261.1, 2032) * mm});
            skSolve(sketch);
        }
        {
            var Q0;
            Q0=makeQuery(id+"F18.imprint","IMPRINT",FACE,{"disambiguationData":[TD([[makeQuery(id+"F18.imprint","IMPRINT",EDGE,{"derivedFrom":sQuery(id+"F18.wireOp",EDGE,"E88")}),1.0]])]});
            extrude(context, id + "F19", {"entities" : qUnion([Q0]), "operationType" : NewBodyOperationType.REMOVE, "oppositeDirection" : true, "depth" : 304.8 * mm, "offsetDistance" : 25.4 * mm});
        }
        {
            var Q0;
            Q0=makeQuery(id+"F17.boolean.opBoolean","MERGE",FACE,{"derivedFrom":[makeQuery(id+"F3.boolean.opBoolean","MERGE",FACE,{"derivedFrom":[makeQuery(id+"F1.opExtrude","SWEPT_FACE",FACE,{"disambiguationData":[OSD([sQuery(id+"F0.wireOp",EDGE,"E43.0")])]}),makeQuery(id+"F1.opExtrude","SWEPT_FACE",FACE,{"disambiguationData":[OSD([sQuery(id+"F0.wireOp",EDGE,"E51")])]}),makeQuery(id+"F3.opExtrude","SWEPT_FACE",FACE,{"disambiguationData":[OSD([sQuery(id+"F2.wireOp",EDGE,"E70.right"),sQuery(id+"F2.wireOp",EDGE,"E71.right")])]})]}),makeQuery(id+"F17.opExtrude","SWEPT_FACE",FACE,{"disambiguationData":[OSD([sQuery(id+"F16.wireOp",EDGE,"E85.right")])]})]});
            var sketch = newSketch(context, id + "F20", { "sketchPlane" : qUnion([Q0])});
            skLineSegment(sketch, "E92.bottom", {"start": v(10061.6, 0) * mm, "end": v(10366.4, 0) * mm});
            skLineSegment(sketch, "E92.top", {"start": v(10061.6, -152.4) * mm, "end": v(10366.4, -152.4) * mm});
            skLineSegment(sketch, "E92.left", {"start": v(10061.6, 0) * mm, "end": v(10061.6, -152.4) * mm});
            skLineSegment(sketch, "E92.right", {"start": v(10366.4, 0) * mm, "end": v(10366.4, -152.4) * mm});
            skSolve(sketch);
        }
        {
            var Q0;
            Q0=makeQuery(id+"F20.imprint","IMPRINT",FACE,{"disambiguationData":[TD([[makeQuery(id+"F20.imprint","IMPRINT",EDGE,{"derivedFrom":sQuery(id+"F20.wireOp",EDGE,"E92.bottom")}),1.0]])]});
            var Q1;
            Q1=makeQuery(id+"F1.opExtrude","SWEPT_FACE",FACE,{"disambiguationData":[OSD([sQuery(id+"F0.wireOp",EDGE,"E47.0")])]});
            extrude(context, id + "F21", {"entities" : qUnion([Q0]), "operationType" : NewBodyOperationType.ADD, "endBound" : BoundingType.UP_TO_SURFACE, "depth" : 25.4 * mm, "endBoundEntityFace" : qUnion([Q1]), "offsetDistance" : 25.4 * mm});
        }
        {
            var Q0;
            Q0=makeQuery(id+"F21.boolean.opBoolean","MERGE",FACE,{"derivedFrom":[makeQuery(id+"F3.boolean.opBoolean","MERGE",FACE,{"derivedFrom":[makeQuery(id+"F1.opExtrude","SWEPT_FACE",FACE,{"disambiguationData":[OSD([sQuery(id+"F0.wireOp",EDGE,"E25"),sQuery(id+"F0.wireOp",EDGE,"E44")])]}),makeQuery(id+"F3.opExtrude","SWEPT_FACE",FACE,{"disambiguationData":[OSD([sQuery(id+"F2.wireOp",EDGE,"E71.bottom")])]})]}),makeQuery(id+"F21.opExtrude","SWEPT_FACE",FACE,{"disambiguationData":[OSD([sQuery(id+"F20.wireOp",EDGE,"E92.right")])]})]});
            var sketch = newSketch(context, id + "F22", { "sketchPlane" : qUnion([Q0])});
            skLineSegment(sketch, "E93.bottom", {"start": v(-4572, 4876.8) * mm, "end": v(165.1, 4876.8) * mm});
            skLineSegment(sketch, "E93.top", {"start": v(-4572, -152.4) * mm, "end": v(165.1, -152.4) * mm});
            skLineSegment(sketch, "E93.left", {"start": v(-4572, 4876.8) * mm, "end": v(-4572, -152.4) * mm});
            skLineSegment(sketch, "E93.right", {"start": v(165.1, 4876.8) * mm, "end": v(165.1, -152.4) * mm});
            skLineSegment(sketch, "E94.bottom", {"start": v(165.1, 0) * mm, "end": v(1079.5, 0) * mm});
            skLineSegment(sketch, "E94.top", {"start": v(165.1, 2032) * mm, "end": v(1079.5, 2032) * mm});
            skLineSegment(sketch, "E94.left", {"start": v(165.1, 0) * mm, "end": v(165.1, 2032) * mm});
            skLineSegment(sketch, "E94.right", {"start": v(1079.5, 0) * mm, "end": v(1079.5, 2032) * mm});
            skSolve(sketch);
        }
        {
            var Q0;
            Q0=makeQuery(id+"F22.imprint","IMPRINT",FACE,{"disambiguationData":[TD([[makeQuery(id+"F22.imprint","IMPRINT",EDGE,{"derivedFrom":sQuery(id+"F22.wireOp",EDGE,"E94.bottom")}),1.0]])]});
            extrude(context, id + "F23", {"entities" : qUnion([Q0]), "operationType" : NewBodyOperationType.REMOVE, "oppositeDirection" : true, "depth" : 304.8 * mm, "offsetDistance" : 25.4 * mm});
        }
        {
            var Q0;
            Q0=makeQuery(id+"F1.opExtrude","SWEPT_FACE",FACE,{"disambiguationData":[OSD([sQuery(id+"F0.wireOp",EDGE,"E62"),sQuery(id+"F0.wireOp",EDGE,"E64")])]});
            var sketch = newSketch(context, id + "F24", { "sketchPlane" : qUnion([Q0])});
            skLineSegment(sketch, "E95", {"start": v(6231.53, 4876.8) * mm, "end": v(6764.93, 4876.8) * mm});
            skLineSegment(sketch, "E96", {"start": v(6764.93, 4876.8) * mm, "end": v(6764.93, 0) * mm});
            skLineSegment(sketch, "E97.bottom", {"start": v(6764.93, 0) * mm, "end": v(6307.73, 0) * mm});
            skLineSegment(sketch, "E97.top", {"start": v(6764.93, 2032) * mm, "end": v(6307.73, 2032) * mm});
            skLineSegment(sketch, "E97.left", {"start": v(6764.93, 0) * mm, "end": v(6764.93, 2032) * mm});
            skLineSegment(sketch, "E97.right", {"start": v(6307.73, 0) * mm, "end": v(6307.73, 2032) * mm});
            skLineSegment(sketch, "E98.bottom", {"start": v(6764.93, 2032) * mm, "end": v(7222.13, 2032) * mm});
            skLineSegment(sketch, "E98.top", {"start": v(6764.93, 0) * mm, "end": v(7222.13, 0) * mm});
            skLineSegment(sketch, "E98.left", {"start": v(6764.93, 2032) * mm, "end": v(6764.93, 0) * mm});
            skLineSegment(sketch, "E98.right", {"start": v(7222.13, 2032) * mm, "end": v(7222.13, 0) * mm});
            skSolve(sketch);
        }
        {
            var Q0;
            Q0=makeQuery(id+"F24.imprint","IMPRINT",FACE,{"disambiguationData":[TD([[makeQuery(id+"F24.imprint","IMPRINT",EDGE,{"derivedFrom":sQuery(id+"F24.wireOp",EDGE,"E98.bottom")}),-1.0]])]});
            var Q1;
            Q1=makeQuery(id+"F24.imprint","IMPRINT",FACE,{"disambiguationData":[TD([[makeQuery(id+"F24.imprint","IMPRINT",EDGE,{"derivedFrom":sQuery(id+"F24.wireOp",EDGE,"E97.bottom")}),1.0]])]});
            extrude(context, id + "F25", {"entities" : qUnion([Q0, Q1]), "operationType" : NewBodyOperationType.REMOVE, "oppositeDirection" : true, "depth" : 114.3 * mm, "offsetDistance" : 25.4 * mm});
        }
        {
            var Q0;
            {var subQ0=makeQuery(id+"F3.opExtrude","CAP_FACE",FACE,{"disambiguationData":[OSD([sQuery(id+"F2.wireOp",EDGE,"E70.right"),sQuery(id+"F2.wireOp",EDGE,"E71.bottom"),sQuery(id+"F2.wireOp",EDGE,"E71.top"),sQuery(id+"F2.wireOp",EDGE,"E71.left"),sQuery(id+"F2.wireOp",EDGE,"E71.right"),sQuery(id+"F2.wireOp",EDGE,"E72.bottom"),sQuery(id+"F2.wireOp",EDGE,"E72.left"),sQuery(id+"F2.wireOp",EDGE,"E72.right"),sQuery(id+"F2.wireOp",EDGE,"E73.trimOffspring")])],"isStart":true});Q0=makeQuery(id+"F25.boolean.opBoolean","MERGE",FACE,{"derivedFrom":[makeQuery(id+"F3.boolean.opBoolean","SPLIT",FACE,{"disambiguationData":[TD([makeQuery(id+"F1.opExtrude","SWEPT_FACE",FACE,{"disambiguationData":[OSD([sQuery(id+"F0.wireOp",EDGE,"E1.left")])]})])],"derivedFrom":subQ0}),makeQuery(id+"F23.boolean.opBoolean","MERGE",FACE,{"derivedFrom":[makeQuery(id+"F3.boolean.opBoolean","SPLIT",FACE,{"disambiguationData":[TD([makeQuery(id+"F1.opExtrude","SWEPT_FACE",FACE,{"disambiguationData":[OSD([sQuery(id+"F0.wireOp",EDGE,"E0.right")])]})])],"derivedFrom":subQ0}),makeQuery(id+"F23.opExtrude","SWEPT_FACE",FACE,{"disambiguationData":[OSD([sQuery(id+"F22.wireOp",EDGE,"E94.bottom")])]})]}),makeQuery(id+"F25.opExtrude","SWEPT_FACE",FACE,{"disambiguationData":[OSD([sQuery(id+"F24.wireOp",EDGE,"E97.bottom"),sQuery(id+"F24.wireOp",EDGE,"E98.top")])]})]});}
            var sketch = newSketch(context, id + "F26", { "sketchPlane" : qUnion([Q0])});
            skLineSegment(sketch, "E99", {"start": v(-800.1, -2140.58) * mm, "end": v(-800.1, 762.41) * mm});
            skLineSegment(sketch, "E100", {"start": v(-800.1, 762.41) * mm, "end": v(-1104.9, 762.41) * mm});
            skLineSegment(sketch, "E101", {"start": v(-1104.9, 762.41) * mm, "end": v(-1104.9, -1835.78) * mm});
            skLineSegment(sketch, "E102", {"start": v(-1104.9, -1835.78) * mm, "end": v(-800.1, -2140.58) * mm});
            skSolve(sketch);
        }
        {
            var Q0;
            Q0=makeQuery(id+"F26.imprint","IMPRINT",FACE,{"disambiguationData":[TD([[makeQuery(id+"F26.imprint","IMPRINT",EDGE,{"derivedFrom":sQuery(id+"F26.wireOp",EDGE,"E99")}),1.0]])]});
            extrude(context, id + "F27", {"entities" : qUnion([Q0]), "operationType" : NewBodyOperationType.ADD, "depth" : 914.4 * mm, "offsetDistance" : 25.4 * mm});
        }
        {
            var Q0;
            Q0=makeQuery(id+"F27.opExtrude","CAP_FACE",FACE,{"disambiguationData":[OSD([sQuery(id+"F26.wireOp",EDGE,"E99"),sQuery(id+"F26.wireOp",EDGE,"E100"),sQuery(id+"F26.wireOp",EDGE,"E101"),sQuery(id+"F26.wireOp",EDGE,"E102")])],"isStart":false});
            var sketch = newSketch(context, id + "F28", { "sketchPlane" : qUnion([Q0])});
            skLineSegment(sketch, "E103.0", {"start": v(-774.7, 787.81) * mm, "end": v(-1130.3, 787.81) * mm});
            skLineSegment(sketch, "E103.1", {"start": v(-774.7, -2201.9) * mm, "end": v(-774.7, 787.81) * mm});
            skLineSegment(sketch, "E103.2", {"start": v(-1130.3, -1846.3) * mm, "end": v(-774.7, -2201.9) * mm});
            skLineSegment(sketch, "E103.3", {"start": v(-1130.3, 787.81) * mm, "end": v(-1130.3, -1846.3) * mm});
            skSolve(sketch);
        }
        {
            var Q0;
            Q0 = qSketchRegion(id + "F28", true);
            extrude(context, id + "F29", {"entities" : qUnion([Q0]), "operationType" : NewBodyOperationType.ADD, "depth" : 38.1 * mm, "offsetDistance" : 25.4 * mm});
        }
        {
            var Q0;
            Q0=makeQuery(id+"F29.opExtrude","CAP_FACE",FACE,{"disambiguationData":[OSD([sQuery(id+"F28.wireOp",EDGE,"E103.0"),sQuery(id+"F28.wireOp",EDGE,"E103.1"),sQuery(id+"F28.wireOp",EDGE,"E103.2"),sQuery(id+"F28.wireOp",EDGE,"E103.3")])],"isStart":false});
            fillet(context, id + "F30", {"entities" : qUnion([Q0]), "radius" : 5.08 * mm, "tangentPropagation" : true, "allowEdgeOverflow" : false});
        }
        {
            var Q0;
            Q0=makeQuery(id+"F29.opExtrude","SWEPT_EDGE",EDGE,{"disambiguationData":[OSD([sQuery(id+"F28.wireOp",EDGE,"E103.0"),sQuery(id+"F28.wireOp",EDGE,"E103.3")])]});
            var Q1;
            Q1=makeQuery(id+"F29.opExtrude","SWEPT_EDGE",EDGE,{"disambiguationData":[OSD([sQuery(id+"F28.wireOp",EDGE,"E103.0"),sQuery(id+"F28.wireOp",EDGE,"E103.1")])]});
            fillet(context, id + "F31", {"entities" : qUnion([Q0, Q1]), "radius" : 5.08 * mm, "tangentPropagation" : true, "allowEdgeOverflow" : false});
        }
    });
